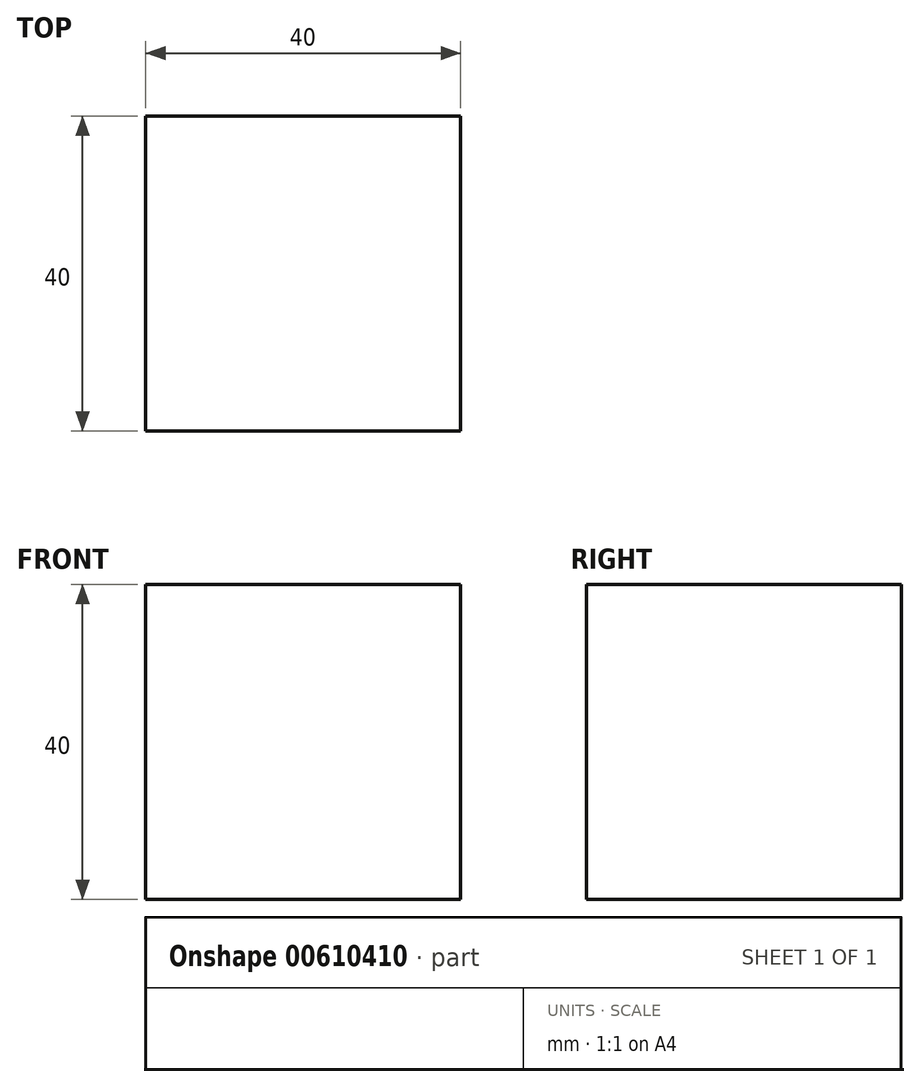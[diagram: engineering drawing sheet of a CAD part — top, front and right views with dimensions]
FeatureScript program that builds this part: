
annotation { "Feature Type Name" : "Feature", "Feature Type Description" : "" }
export const myFeature = defineFeature(function(context is Context, id is Id, definition is map)
    precondition{}
    {
        {
            var Q0;
            Q0=qCreatedBy(makeId("Top.planeOp"),FACE);
            var sketch = newSketch(context, id + "F0", { "sketchPlane" : qUnion([Q0])});
            skLineSegment(sketch, "E0.bottom", {"start": v(0, 0) * mm, "end": v(-40, 0) * mm});
            skLineSegment(sketch, "E0.top", {"start": v(0, 40) * mm, "end": v(-40, 40) * mm});
            skLineSegment(sketch, "E0.left", {"start": v(0, 0) * mm, "end": v(0, 40) * mm});
            skLineSegment(sketch, "E0.right", {"start": v(-40, 0) * mm, "end": v(-40, 40) * mm});
            skSolve(sketch);
        }
        {
            var Q0;
            Q0=makeQuery(id+"F0.imprint","IMPRINT",FACE,{"disambiguationData":[TD([[makeQuery(id+"F0.imprint","IMPRINT",EDGE,{"derivedFrom":sQuery(id+"F0.wireOp",EDGE,"E0.bottom")}),-1.0]])]});
            extrude(context, id + "F1", {"entities" : qUnion([Q0]), "depth" : 40 * mm, "offsetDistance" : 25 * mm});
        }
    });
